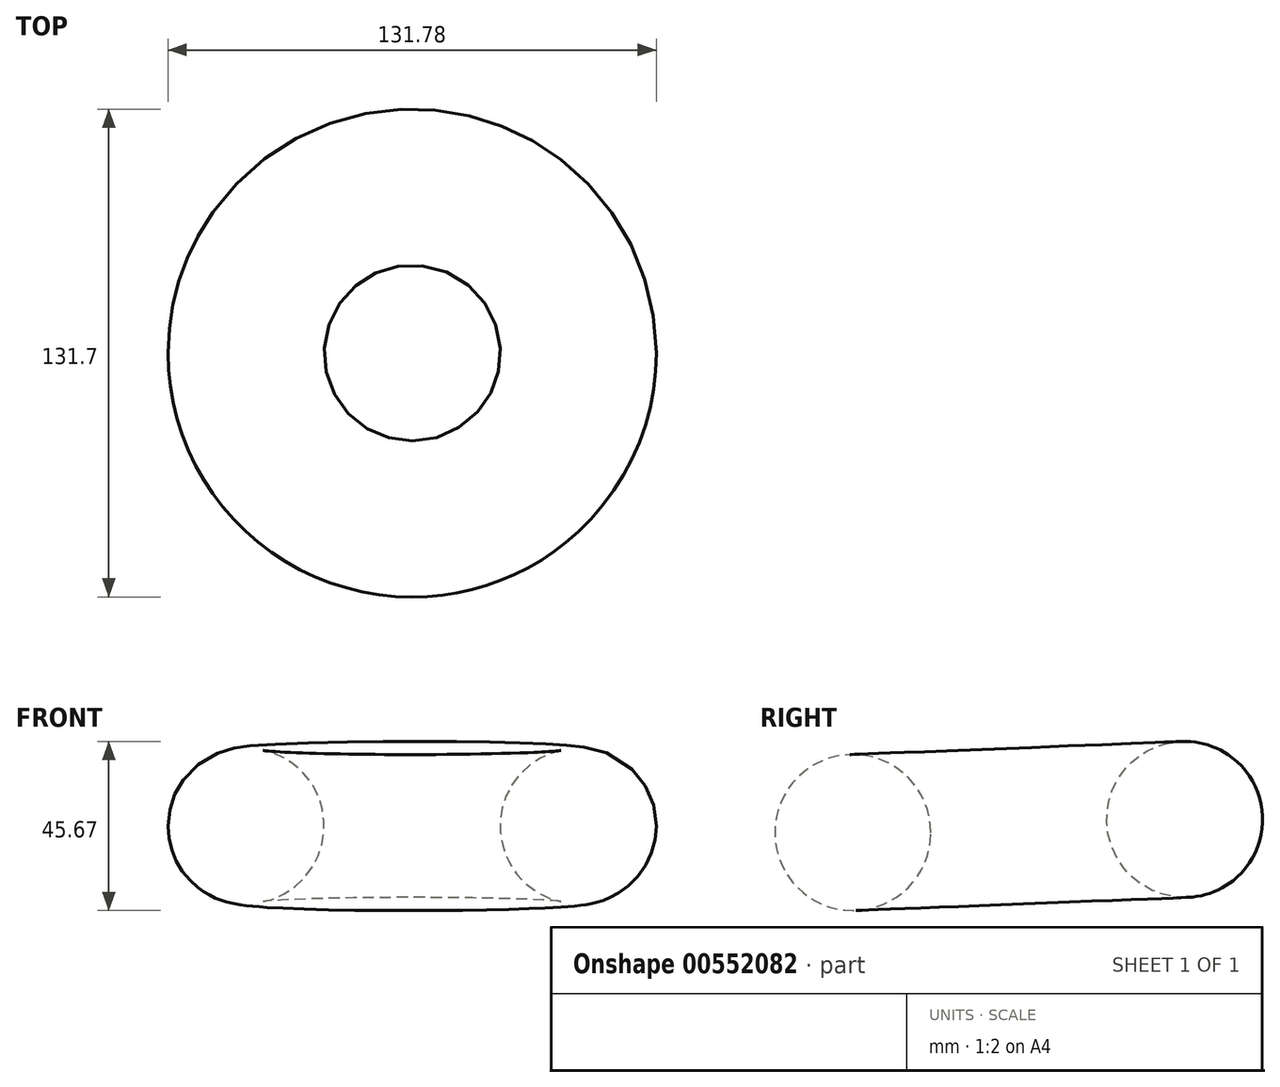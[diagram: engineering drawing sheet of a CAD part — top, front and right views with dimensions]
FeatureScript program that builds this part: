
annotation { "Feature Type Name" : "Feature", "Feature Type Description" : "" }
export const myFeature = defineFeature(function(context is Context, id is Id, definition is map)
    precondition{}
    {
        {
            var Q0;
            Q0=qCreatedBy(makeId("Right.planeOp"),FACE);
            var sketch = newSketch(context, id + "F0", { "sketchPlane" : qUnion([Q0])});
            skLineSegment(sketch, "E0", {"start": v(-52.55, 49.69) * mm, "end": v(-52.55, -46.05) * mm});
            skCircle(sketch, "E1", {"center": v(0, 0) * mm, "radius": 21.06 * mm});
            skSolve(sketch);
        }
        {
            var Q0;
            Q0=qCreatedBy(makeId("Right.planeOp"),FACE);
            var sketch = newSketch(context, id + "F1", { "sketchPlane" : qUnion([Q0])});
            skLineSegment(sketch, "E2", {"start": v(-46.83, 49.8) * mm, "end": v(-42.84, -51.13) * mm});
            skSolve(sketch);
        }
        {
            var Q0;
            Q0=makeQuery(id+"F0.imprint","IMPRINT",FACE,{"disambiguationData":[TD([[makeQuery(id+"F0.imprint","IMPRINT",EDGE,{"derivedFrom":sQuery(id+"F0.wireOp",EDGE,"E1")}),1.0]])]});
            var Q1;
            Q1=sQuery(id+"F1.wireOp",EDGE,"E2");
            revolve(context, id + "F2", {"entities" : qUnion([Q0]), "axis" : qUnion([Q1]), "revolveType" : RevolveType.FULL});
        }
    });
